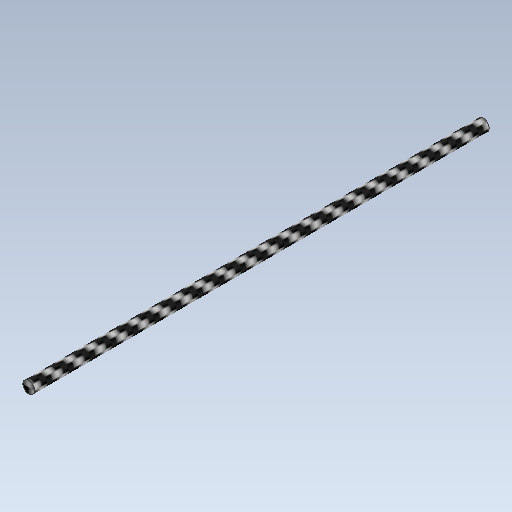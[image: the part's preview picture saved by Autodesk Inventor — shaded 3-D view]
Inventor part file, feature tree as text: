
AUTODESK INVENTOR PART (.ipt)
format: ipt  version: 2020 (Build 240168000, 168)  size: 104,960 bytes
history: native  units: in
note: dims shown in document units (in); Inventor stores cm internally (conversion verified against a paired STEP export)
features: extrude x1, sketch x1
ambient origin geometry x8: Origin, YZ Plane, XZ Plane, XY Plane, X Axis, Y Axis, Z Axis, Center Point
bodies: Solid1 (feature_tree)
feature tree (2):
  extrude  "Extrusion1"  Depth=3.1106in
  sketch  "Sketch1"  dims[d0=0.0827in d1=3.1106in d2=0.0in]
